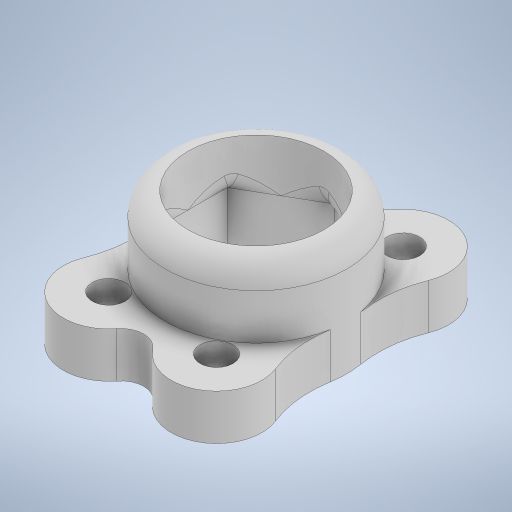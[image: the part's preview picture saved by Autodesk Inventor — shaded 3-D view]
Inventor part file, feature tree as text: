
AUTODESK INVENTOR PART (.ipt)
format: ipt  version: 2023 (Build 270158000, 158)  size: 477,184 bytes
history: native  units: mm
features: sketch x5, extrude x4, fillet x4, hole x1, projected_geometry x1
ambient origin geometry x8: Origin, YZ Plane, XZ Plane, XY Plane, X Axis, Y Axis, Z Axis, Center Point
bodies: Solid1 (feature_tree)
feature tree (15):
  extrude  "Extrusion1"  Depth=9.5mm
  extrude  "Extrusion2"  Depth=9.5mm
  extrude  "Extrusion3"  Depth=8.0mm
  extrude  "Extrusion4"  Depth=4.0mm TaperAngle=0.0deg
  fillet  "Fillet1"  Radius=6.0mm
  hole  "Hole1"  [1 undecoded]
  fillet  "Fillet2"  Radius=12.0mm
  fillet  "Fillet4"  Radius=5.5mm
  fillet  "Fillet5"  Radius=2.0mm
  sketch  "Sketch1"  dims[d0=8.0mm d1=8.0mm d2=9.5mm]
  sketch  "Sketch2"  dims[d3=8.0mm d5=9.5mm]
  sketch  "Sketch3"  dims[d9=8.0mm d10=8.0mm]
  sketch  "Sketch4"  dims[d11=16.0mm d13=4.0mm d14=0.0mm d15=6.0mm d16=0.0mm]
  sketch  "Sketch5"  dims[d17=12.0mm d18=6.0mm d19=0.0mm d20=12.0mm d21=5.5mm d22=0.0mm d23=2.0mm d24=2.9mm d25=6.0mm d26=5.5mm d27=2.0mm d28=90.0deg d29=8.0mm d30=20.594885mm d31=2.0mm d33=2.0mm d34=10.0mm]
  projected_geometry  "Projected Loop1"
note: 1 required parameter value undecoded (feature->parameter linkage not recoverable at this tier; creation-order binding heuristic only, values carry confidence <= 0.55)
